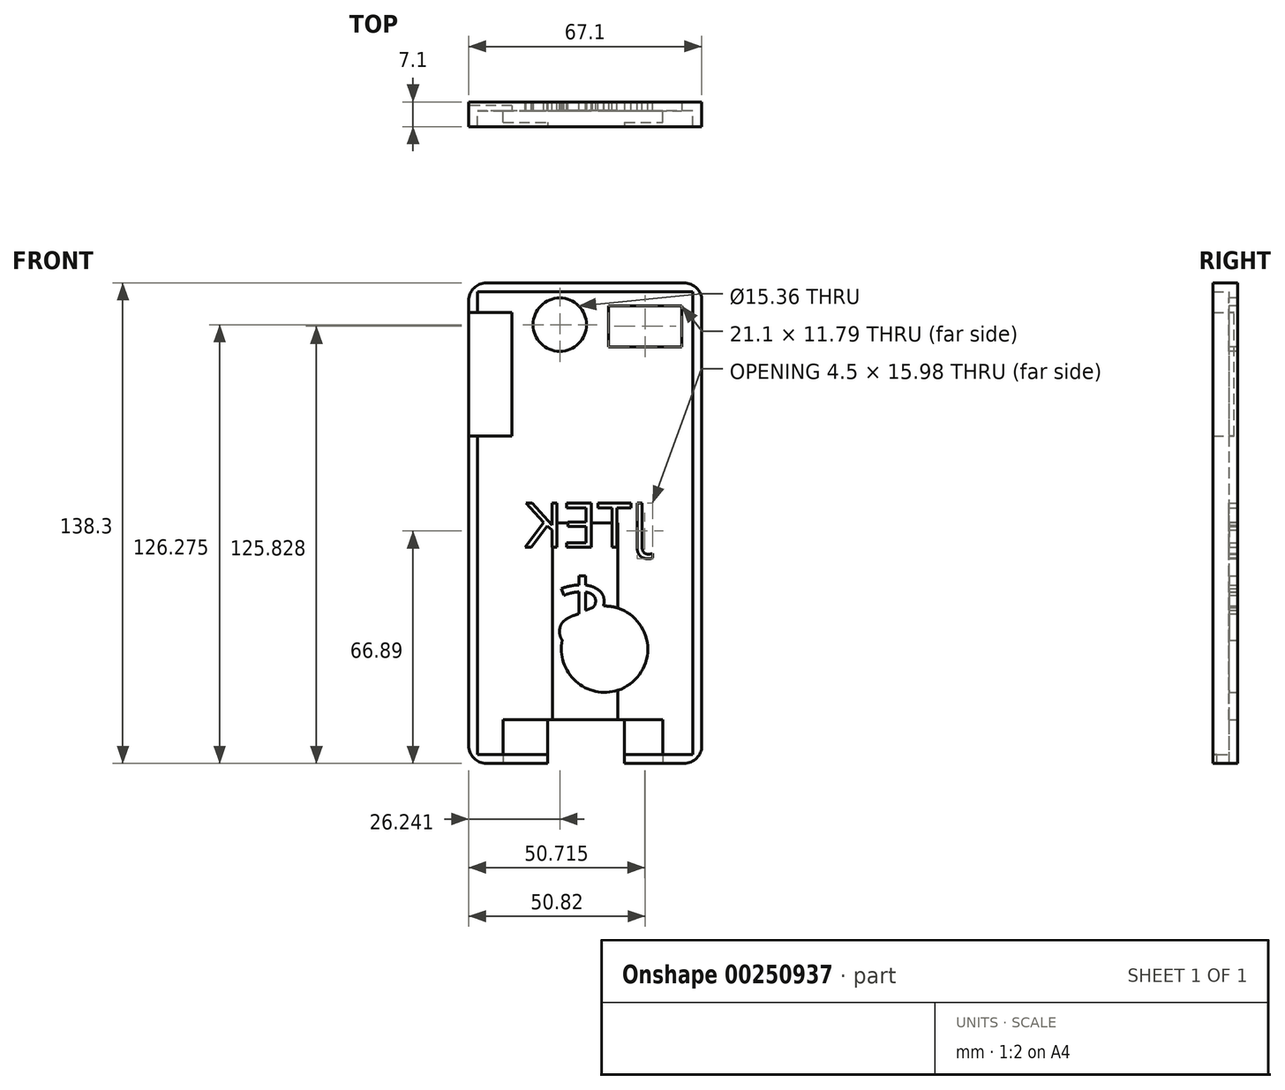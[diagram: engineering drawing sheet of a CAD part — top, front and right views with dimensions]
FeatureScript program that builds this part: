
annotation { "Feature Type Name" : "Feature", "Feature Type Description" : "" }
export const myFeature = defineFeature(function(context is Context, id is Id, definition is map)
    precondition{}
    {
        {
            var Q0;
            Q0=qCreatedBy(makeId("Front.planeOp"),FACE);
            var sketch = newSketch(context, id + "F0", { "sketchPlane" : qUnion([Q0])});
            skLineSegment(sketch, "E0.bottom", {"start": v(33.55, 69.15) * mm, "end": v(-33.55, 69.15) * mm});
            skLineSegment(sketch, "E0.top", {"start": v(33.55, -69.15) * mm, "end": v(-33.55, -69.15) * mm});
            skLineSegment(sketch, "E0.left", {"start": v(33.55, 69.15) * mm, "end": v(33.55, -69.15) * mm});
            skLineSegment(sketch, "E0.right", {"start": v(-33.55, 69.15) * mm, "end": v(-33.55, -69.15) * mm});
            skPoint(sketch, "E0.middle", {"position": v(0, 0) * mm});
            skSolve(sketch);
        }
        {
            var Q0;
            Q0=makeQuery(id+"F0.imprint","IMPRINT",FACE,{"disambiguationData":[TD([[makeQuery(id+"F0.imprint","IMPRINT",EDGE,{"derivedFrom":sQuery(id+"F0.wireOp",EDGE,"E0.bottom")}),1.0]])]});
            extrude(context, id + "F1", {"entities" : qUnion([Q0]), "endBound" : BoundingType.SYMMETRIC, "depth" : 7.1 * mm});
        }
        {
            var Q0;
            Q0=makeQuery(id+"F1.opExtrude","CAP_FACE",FACE,{"disambiguationData":[OSD([sQuery(id+"F0.wireOp",EDGE,"E0.bottom"),sQuery(id+"F0.wireOp",EDGE,"E0.top"),sQuery(id+"F0.wireOp",EDGE,"E0.left"),sQuery(id+"F0.wireOp",EDGE,"E0.right")])],"isStart":false});
            shell(context, id + "F2", {"entities" : qUnion([Q0]), "thickness" : 2.54 * mm});
        }
        {
            var Q0;
            Q0=makeQuery(id+"F1.opExtrude","SWEPT_EDGE",EDGE,{"disambiguationData":[OSD([sQuery(id+"F0.wireOp",EDGE,"E0.bottom"),sQuery(id+"F0.wireOp",EDGE,"E0.left")])]});
            fillet(context, id + "F3", {"entities" : qUnion([Q0]), "radius" : 5.08 * mm, "tangentPropagation" : true, "allowEdgeOverflow" : false});
        }
        {
            var Q0;
            Q0=makeQuery(id+"F1.opExtrude","SWEPT_EDGE",EDGE,{"disambiguationData":[OSD([sQuery(id+"F0.wireOp",EDGE,"E0.bottom"),sQuery(id+"F0.wireOp",EDGE,"E0.right")])]});
            fillet(context, id + "F4", {"entities" : qUnion([Q0]), "radius" : 5.08 * mm, "tangentPropagation" : true, "allowEdgeOverflow" : false});
        }
        {
            var Q0;
            Q0=makeQuery(id+"F1.opExtrude","SWEPT_EDGE",EDGE,{"disambiguationData":[OSD([sQuery(id+"F0.wireOp",EDGE,"E0.top"),sQuery(id+"F0.wireOp",EDGE,"E0.right")])]});
            fillet(context, id + "F5", {"entities" : qUnion([Q0]), "radius" : 5.08 * mm, "tangentPropagation" : true, "allowEdgeOverflow" : false});
        }
        {
            var Q0;
            Q0=makeQuery(id+"F1.opExtrude","SWEPT_EDGE",EDGE,{"disambiguationData":[OSD([sQuery(id+"F0.wireOp",EDGE,"E0.top"),sQuery(id+"F0.wireOp",EDGE,"E0.left")])]});
            fillet(context, id + "F6", {"entities" : qUnion([Q0]), "radius" : 5.08 * mm, "tangentPropagation" : true, "allowEdgeOverflow" : false});
        }
        {
            var Q0;
            Q0=makeQuery(id+"F2.opShell","OFFSET_FACE",FACE,{"disambiguationData":[OSD([sQuery(id+"F0.wireOp",EDGE,"E0.bottom"),sQuery(id+"F0.wireOp",EDGE,"E0.top"),sQuery(id+"F0.wireOp",EDGE,"E0.left"),sQuery(id+"F0.wireOp",EDGE,"E0.right")])]});
            var sketch = newSketch(context, id + "F7", { "sketchPlane" : qUnion([Q0])});
            skLineSegment(sketch, "E1.bottom", {"start": v(6.72, 62.57) * mm, "end": v(27.82, 62.57) * mm});
            skLineSegment(sketch, "E1.top", {"start": v(6.72, 50.78) * mm, "end": v(27.82, 50.78) * mm});
            skLineSegment(sketch, "E1.left", {"start": v(6.72, 62.57) * mm, "end": v(6.72, 50.78) * mm});
            skLineSegment(sketch, "E1.right", {"start": v(27.82, 62.57) * mm, "end": v(27.82, 50.78) * mm});
            skSolve(sketch);
        }
        {
            var Q0;
            Q0=makeQuery(id+"F7.imprint","IMPRINT",FACE,{"disambiguationData":[TD([[makeQuery(id+"F7.imprint","IMPRINT",EDGE,{"derivedFrom":sQuery(id+"F7.wireOp",EDGE,"E1.bottom")}),-1.0]])]});
            extrude(context, id + "F8", {"entities" : qUnion([Q0]), "operationType" : NewBodyOperationType.REMOVE, "endBound" : BoundingType.SYMMETRIC, "oppositeDirection" : true, "depth" : 25 * mm});
        }
        {
            var Q0;
            Q0=makeQuery(id+"F1.opExtrude","SWEPT_FACE",FACE,{"disambiguationData":[OSD([sQuery(id+"F0.wireOp",EDGE,"E0.top")])]});
            var sketch = newSketch(context, id + "F9", { "sketchPlane" : qUnion([Q0])});
            skLineSegment(sketch, "E2.bottom", {"start": v(-10.88, 3.55) * mm, "end": v(11.32, 3.55) * mm});
            skLineSegment(sketch, "E2.top", {"start": v(-10.88, -3.55) * mm, "end": v(11.32, -3.55) * mm});
            skLineSegment(sketch, "E2.left", {"start": v(-10.88, 3.55) * mm, "end": v(-10.88, -3.55) * mm});
            skLineSegment(sketch, "E2.right", {"start": v(11.32, 3.55) * mm, "end": v(11.32, -3.55) * mm});
            skSolve(sketch);
        }
        {
            var Q0;
            Q0=makeQuery(id+"F9.imprint","IMPRINT",FACE,{"disambiguationData":[TD([[makeQuery(id+"F9.imprint","IMPRINT",EDGE,{"derivedFrom":sQuery(id+"F9.wireOp",EDGE,"E2.bottom")}),1.0]])]});
            extrude(context, id + "F10", {"entities" : qUnion([Q0]), "operationType" : NewBodyOperationType.REMOVE, "endBound" : BoundingType.SYMMETRIC, "depth" : 25 * mm});
        }
        {
            var Q0;
            Q0=qCreatedBy(makeId("Top.planeOp"),FACE);
            var sketch = newSketch(context, id + "F11", { "sketchPlane" : qUnion([Q0])});
            skLineSegment(sketch, "E3.bottom", {"start": v(9.4, -1.11) * mm, "end": v(-9.4, -1.11) * mm});
            skLineSegment(sketch, "E3.top", {"start": v(9.4, 1.11) * mm, "end": v(-9.4, 1.11) * mm});
            skLineSegment(sketch, "E3.left", {"start": v(9.4, -1.11) * mm, "end": v(9.4, 1.11) * mm});
            skLineSegment(sketch, "E3.right", {"start": v(-9.4, -1.11) * mm, "end": v(-9.4, 1.11) * mm});
            skPoint(sketch, "E3.middle", {"position": v(0, 0) * mm});
            skSolve(sketch);
        }
        {
            var Q0;
            Q0=makeQuery(id+"F11.imprint","IMPRINT",FACE,{"disambiguationData":[TD([[makeQuery(id+"F11.imprint","IMPRINT",EDGE,{"derivedFrom":sQuery(id+"F11.wireOp",EDGE,"E3.bottom")}),-1.0]])]});
            extrude(context, id + "F12", {"entities" : qUnion([Q0]), "operationType" : NewBodyOperationType.REMOVE, "oppositeDirection" : true, "depth" : 91.3 * mm});
        }
        {
            var Q0;
            Q0=makeQuery(id+"F1.opExtrude","SWEPT_FACE",FACE,{"disambiguationData":[OSD([sQuery(id+"F0.wireOp",EDGE,"E0.right")])]});
            var sketch = newSketch(context, id + "F13", { "sketchPlane" : qUnion([Q0])});
            skLineSegment(sketch, "E4.bottom", {"start": v(-2.53, 60.66) * mm, "end": v(3.55, 60.66) * mm});
            skLineSegment(sketch, "E4.top", {"start": v(-2.53, 37.82) * mm, "end": v(3.55, 37.82) * mm});
            skLineSegment(sketch, "E4.left", {"start": v(-2.53, 60.66) * mm, "end": v(-2.53, 37.82) * mm});
            skLineSegment(sketch, "E4.right", {"start": v(3.55, 60.66) * mm, "end": v(3.55, 37.82) * mm});
            skSolve(sketch);
        }
        {
            var Q0;
            Q0=makeQuery(id+"F13.imprint","IMPRINT",FACE,{"disambiguationData":[TD([[makeQuery(id+"F13.imprint","IMPRINT",EDGE,{"derivedFrom":sQuery(id+"F13.wireOp",EDGE,"E4.bottom")}),-1.0]])]});
            extrude(context, id + "F14", {"entities" : qUnion([Q0]), "operationType" : NewBodyOperationType.REMOVE, "endBound" : BoundingType.SYMMETRIC, "oppositeDirection" : true, "depth" : 25 * mm});
        }
        {
            var Q0;
            Q0=makeQuery(id+"F2.opShell","OFFSET_FACE",FACE,{"disambiguationData":[OSD([sQuery(id+"F0.wireOp",EDGE,"E0.bottom"),sQuery(id+"F0.wireOp",EDGE,"E0.top"),sQuery(id+"F0.wireOp",EDGE,"E0.left"),sQuery(id+"F0.wireOp",EDGE,"E0.right")])]});
            var sketch = newSketch(context, id + "F15", { "sketchPlane" : qUnion([Q0])});
            skCircle(sketch, "E5", {"center": v(-7.3, 57.13) * mm, "radius": 7.68 * mm});
            skSolve(sketch);
        }
        {
            var Q0;
            Q0=makeQuery(id+"F15.imprint","IMPRINT",FACE,{"disambiguationData":[TD([[makeQuery(id+"F15.imprint","IMPRINT",EDGE,{"derivedFrom":sQuery(id+"F15.wireOp",EDGE,"E5")}),1.0]])]});
            extrude(context, id + "F16", {"entities" : qUnion([Q0]), "operationType" : NewBodyOperationType.REMOVE, "oppositeDirection" : true, "depth" : 25 * mm});
        }
        {
            var Q0;
            Q0=makeQuery(id+"F1.opExtrude","SWEPT_FACE",FACE,{"disambiguationData":[OSD([sQuery(id+"F0.wireOp",EDGE,"E0.top")])]});
            var sketch = newSketch(context, id + "F17", { "sketchPlane" : qUnion([Q0])});
            skPoint(sketch, "E6.oppositeSnap0", {"position": v(0, -1.11) * mm});
            skLineSegment(sketch, "E6.bottom", {"start": v(-23.58, 2.37) * mm, "end": v(22.34, 2.37) * mm});
            skLineSegment(sketch, "E6.top", {"start": v(-23.58, -1.11) * mm, "end": v(22.34, -1.11) * mm});
            skLineSegment(sketch, "E6.left", {"start": v(-23.58, 2.37) * mm, "end": v(-23.58, -1.11) * mm});
            skLineSegment(sketch, "E6.right", {"start": v(22.34, 2.37) * mm, "end": v(22.34, -1.11) * mm});
            skSolve(sketch);
        }
        {
            var Q0;
            Q0=makeQuery(id+"F17.imprint","IMPRINT",FACE,{"disambiguationData":[TD([[makeQuery(id+"F17.imprint","IMPRINT",EDGE,{"derivedFrom":sQuery(id+"F17.wireOp",EDGE,"E6.bottom")}),-1.0]])]});
            extrude(context, id + "F18", {"entities" : qUnion([Q0]), "operationType" : NewBodyOperationType.REMOVE, "endBound" : BoundingType.SYMMETRIC, "oppositeDirection" : true, "depth" : 25 * mm});
        }
        {
            var Q0;
            Q0=makeQuery(id+"F1.opExtrude","SWEPT_FACE",FACE,{"disambiguationData":[OSD([sQuery(id+"F0.wireOp",EDGE,"E0.right")])]});
            var sketch = newSketch(context, id + "F19", { "sketchPlane" : qUnion([Q0])});
            skLineSegment(sketch, "E7.bottom", {"start": v(-2.53, 37.82) * mm, "end": v(4.57, 37.82) * mm});
            skLineSegment(sketch, "E7.top", {"start": v(-2.53, 25.03) * mm, "end": v(4.57, 25.03) * mm});
            skLineSegment(sketch, "E7.left", {"start": v(-2.53, 37.82) * mm, "end": v(-2.53, 25.03) * mm});
            skLineSegment(sketch, "E7.right", {"start": v(4.57, 37.82) * mm, "end": v(4.57, 25.03) * mm});
            skSolve(sketch);
        }
        {
            var Q0;
            {var subQ0=sQuery(id+"F19.wireOp",EDGE,"E7.left");Q0=makeQuery(id+"F19.imprint","IMPRINT",FACE,{"disambiguationData":[TD([[makeQuery(id+"F19.imprint","IMPRINT",EDGE,{"derivedFrom":subQ0}),1.0]])]});}
            extrude(context, id + "F20", {"entities" : qUnion([Q0]), "operationType" : NewBodyOperationType.REMOVE, "endBound" : BoundingType.SYMMETRIC, "oppositeDirection" : true, "depth" : 25 * mm});
        }
        {
            var Q0;
            Q0=makeQuery(id+"F1.opExtrude","CAP_FACE",FACE,{"disambiguationData":[OSD([sQuery(id+"F0.wireOp",EDGE,"E0.bottom"),sQuery(id+"F0.wireOp",EDGE,"E0.top"),sQuery(id+"F0.wireOp",EDGE,"E0.left"),sQuery(id+"F0.wireOp",EDGE,"E0.right")])],"isStart":true});
            var sketch = newSketch(context, id + "F21", { "sketchPlane" : qUnion([Q0])});
            skLineSegment(sketch, "E8", {"start": v(-29.02, 12.37) * mm, "end": v(-20.7, 12.37) * mm});
            skLineSegment(sketch, "E9", {"start": v(-24.86, 12.37) * mm, "end": v(-24.86, 0) * mm});
            skLineSegment(sketch, "E10", {"start": v(-10.91, 12.37) * mm, "end": v(-17.14, 12.37) * mm});
            skLineSegment(sketch, "E11", {"start": v(-17.14, 12.37) * mm, "end": v(-17.14, 5.55) * mm});
            skLineSegment(sketch, "E12", {"start": v(-17.14, 5.55) * mm, "end": v(-10.02, 5.55) * mm});
            skLineSegment(sketch, "E13", {"start": v(-17.14, 5.55) * mm, "end": v(-17.14, 0) * mm});
            skLineSegment(sketch, "E14", {"start": v(-17.14, 0) * mm, "end": v(-10.02, 0) * mm});
            skLineSegment(sketch, "E15", {"start": v(-4.09, 12.37) * mm, "end": v(-4.09, 0) * mm});
            skLineSegment(sketch, "E16", {"start": v(-4.09, 6.19) * mm, "end": v(2.15, 10) * mm});
            skLineSegment(sketch, "E17", {"start": v(-4.09, 6.19) * mm, "end": v(0, 0) * mm});
            skLineSegment(sketch, "E18", {"start": v(10.45, 12.37) * mm, "end": v(17.58, 12.37) * mm});
            skLineSegment(sketch, "E19", {"start": v(17.58, 12.37) * mm, "end": v(17.58, 6.19) * mm});
            skLineSegment(sketch, "E20", {"start": v(17.58, 6.19) * mm, "end": v(9.56, 5.55) * mm});
            skLineSegment(sketch, "E21", {"start": v(9.56, 5.55) * mm, "end": v(10, 0) * mm});
            skLineSegment(sketch, "E22", {"start": v(10, 0) * mm, "end": v(17.58, 0.6) * mm});
            skLineSegment(sketch, "E23", {"start": v(24.4, 10) * mm, "end": v(24.4, -3.36) * mm});
            skCircle(sketch, "E24", {"center": v(-5.57, -36.3) * mm, "radius": 12.43 * mm});
            skSolve(sketch);
        }
        {
            var Q0;
            Q0 = qSketchRegion(id + "F21", true);
            extrude(context, id + "F22", {"entities" : qUnion([Q0]), "depth" : 25 * mm});
        }
        {
            var Q0;
            Q0=makeQuery(id+"F22.opExtrude","CAP_FACE",FACE,{"disambiguationData":[OSD([sQuery(id+"F21.wireOp",EDGE,"E24")])],"isStart":false});
            extrude(context, id + "F23", {"entities" : qUnion([Q0]), "operationType" : NewBodyOperationType.REMOVE, "endBound" : BoundingType.SYMMETRIC, "oppositeDirection" : true, "depth" : 217.2 * mm});
        }
        {
            var Q0;
            Q0=makeQuery(id+"F1.opExtrude","CAP_FACE",FACE,{"disambiguationData":[OSD([sQuery(id+"F0.wireOp",EDGE,"E0.bottom"),sQuery(id+"F0.wireOp",EDGE,"E0.top"),sQuery(id+"F0.wireOp",EDGE,"E0.left"),sQuery(id+"F0.wireOp",EDGE,"E0.right")])],"isStart":true});
            var sketch = newSketch(context, id + "F24", { "sketchPlane" : qUnion([Q0])});
            skText(sketch, "E25", { "text": "JTEK", "fontName": "OpenSans-Regular.ttf"});
            const initialGuessF24  = {"E25": [-0.01803, -0.00692, 1, 0, 0.01276]};
            skSetInitialGuess(sketch, initialGuessF24);
            skSolve(sketch);
        }
        {
            var Q0;
            Q0 = qSketchRegion(id + "F24", true);
            extrude(context, id + "F25", {"entities" : qUnion([Q0]), "operationType" : NewBodyOperationType.REMOVE, "endBound" : BoundingType.SYMMETRIC, "oppositeDirection" : true, "depth" : 25 * mm});
        }
        {
            var Q0;
            Q0=makeQuery(id+"F1.opExtrude","CAP_FACE",FACE,{"disambiguationData":[OSD([sQuery(id+"F0.wireOp",EDGE,"E0.bottom"),sQuery(id+"F0.wireOp",EDGE,"E0.top"),sQuery(id+"F0.wireOp",EDGE,"E0.left"),sQuery(id+"F0.wireOp",EDGE,"E0.right")])],"isStart":true});
            var sketch = newSketch(context, id + "F26", { "sketchPlane" : qUnion([Q0])});
            skText(sketch, "E26", { "text": "$", "fontName": "OpenSans-Regular.ttf"});
            const initialGuessF26  = {"E26": [-0.0076, -0.0377, 1, 0, 0.02133]};
            skSetInitialGuess(sketch, initialGuessF26);
            skSolve(sketch);
        }
        {
            var Q0;
            Q0 = qSketchRegion(id + "F26", true);
            extrude(context, id + "F27", {"entities" : qUnion([Q0]), "operationType" : NewBodyOperationType.REMOVE, "oppositeDirection" : true, "depth" : 25 * mm});
        }
    });
